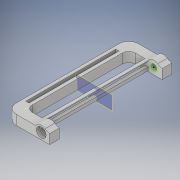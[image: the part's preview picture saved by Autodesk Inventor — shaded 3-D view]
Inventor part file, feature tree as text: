
AUTODESK INVENTOR PART (.ipt)
format: ipt  version: 2018 (Build 220112000, 112)  size: 229,376 bytes
history: native  units: in
note: dims shown in document units (in); Inventor stores cm internally (conversion verified against a paired STEP export)
features: sketch x15, extrude x9, fillet x6, hole x2, plane x1, mirror x1
ambient origin geometry x8: Origin, YZ Plane, XZ Plane, XY Plane, X Axis, Y Axis, Z Axis, Center Point
bodies: Solid1 (feature_tree)
feature tree (34):
  extrude  "Extrusion1"  Depth=0.375in
  sketch  "Sketch2"  dims[d3=0.375in d4=0.5in d5=0.375in d6=0.0in]
  extrude  "Extrusion2"  Depth=0.375in
  fillet  "Fillet1"  Radius=0.375in
  extrude  "Extrusion3"  Depth=0.375in
  extrude  "Extrusion4"  Depth=0.25in
  plane  "Work Plane1"
  mirror  "Mirror1"
  fillet  "Fillet2"  Radius=0.24in
  extrude  "Extrusion5"  Depth=0.375in
  sketch  "Sketch6"  dims[d17=1.0in d18=0.0in d19=0.24in d20=0.0in]
  extrude  "Extrusion6"  Depth=0.24in TaperAngle=0.0deg
  extrude  "Extrusion7"  Depth=0.375in
  fillet  "Fillet3"  Radius=0.25in
  fillet  "Fillet4"  Radius=0.375in
  fillet  "Fillet5"  Radius=0.25in
  fillet  "Fillet6"  Radius=0.125in
  sketch  "Sketch9"  dims[d30=0.125in d31=0.125in]
  extrude  "Extrusion8"  Depth=0.035in
  sketch  "Sketch11"  dims[d35=0.2in]
  sketch  "Sketch12"  dims[d36=0.2in d37=0.75in d38=0.375in d39=0.25in d40=0.5635in d41=0.35in d42=0.0in]
  hole  "Hole1"  [1 undecoded]
  hole  "Hole2"  [1 undecoded]
  sketch  "Sketch14"  dims[d51=3.5in]
  extrude  "Extrusion9"  Depth=0.125in
  sketch  "Sketch1"  dims[d0=1.3in d1=0.375in]
  sketch  "Sketch3"  dims[d7=0.375in d8=0.0in d9=0.375in]
  sketch  "Sketch4"  dims[d10=0.24in d11=0.0in d12=0.25in d13=0.24in d14=0.0in]
  sketch  "Sketch5"  dims[d15=2.0in d16=0.375in]
  sketch  "Sketch7"  dims[d21=0.375in d22=0.0in d23=0.375in d24=0.25in d25=0.375in d26=0.25in d27=0.125in]
  sketch  "Sketch8"  dims[d28=0.035in d29=0.035in]
  sketch  "Sketch10"  dims[d32=4.375in d33=0.0in d34=0.2in]
  sketch  "Sketch13"  dims[d43=0.2in d44=0.75in d45=0.375in d46=0.25in d47=0.5635in d48=0.35in d49=0.0in d50=0.125in]
  sketch  "Sketch15"  dims[d52=0.375in d53=0.0in]
note: 2 required parameter values undecoded (feature->parameter linkage not recoverable at this tier; creation-order binding heuristic only, values carry confidence <= 0.55)
